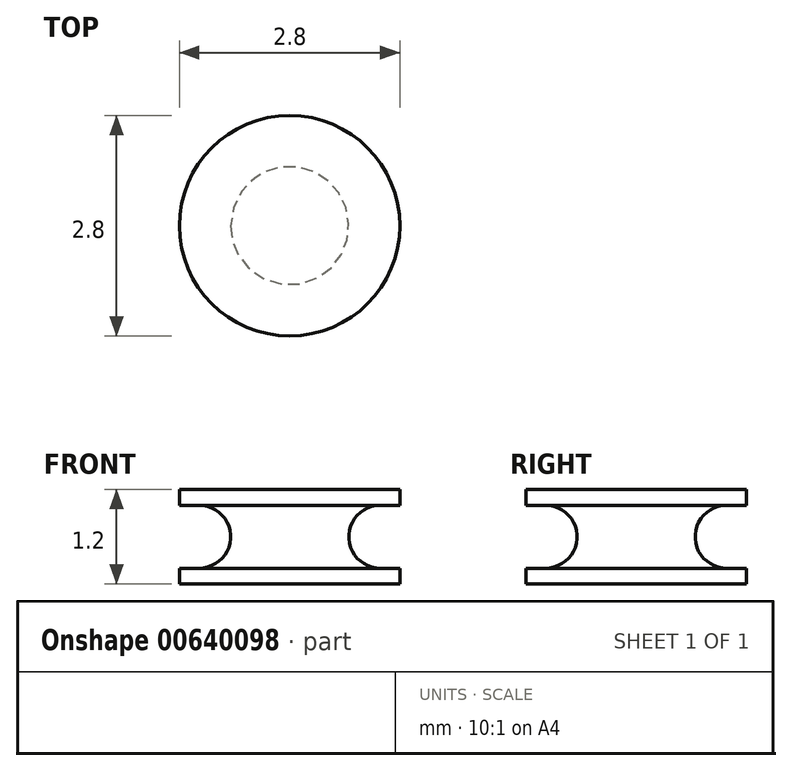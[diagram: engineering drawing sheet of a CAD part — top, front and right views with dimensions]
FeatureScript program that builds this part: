
annotation { "Feature Type Name" : "Feature", "Feature Type Description" : "" }
export const myFeature = defineFeature(function(context is Context, id is Id, definition is map)
    precondition{}
    {
        {
            var Q0;
            Q0=qCreatedBy(makeId("Front.planeOp"),FACE);
            var sketch = newSketch(context, id + "F0", { "sketchPlane" : qUnion([Q0])});
            skLineSegment(sketch, "E0.top", {"start": v(0, 0.6) * mm, "end": v(1.4, 0.6) * mm});
            skLineSegment(sketch, "E0.left", {"start": v(0, 0) * mm, "end": v(0, 0.6) * mm});
            skLineSegment(sketch, "E0.right", {"start": v(1.4, 0.4) * mm, "end": v(1.4, 0.6) * mm});
            skArc(sketch, "E1", {"start": v(1.15, 0.4) * mm, "mid": v(0.87, 0.28) * mm, "end": v(0.75, 0) * mm});
            skLineSegment(sketch, "E2", {"start": v(1.15, 0.4) * mm, "end": v(1.4, 0.4) * mm});
            skLineSegment(sketch, "E3.MirrorCS", {"start": v(0, -0.6) * mm, "end": v(1.4, -0.6) * mm});
            skLineSegment(sketch, "E4.MirrorCS", {"start": v(0, 0) * mm, "end": v(0, -0.6) * mm});
            skLineSegment(sketch, "E5.MirrorCS", {"start": v(1.15, -0.4) * mm, "end": v(1.4, -0.4) * mm});
            skArc(sketch, "E6.MirrorCS", {"start": v(1.15, -0.4) * mm, "mid": v(0.87, -0.28) * mm, "end": v(0.75, 0) * mm});
            skLineSegment(sketch, "E7.MirrorCS", {"start": v(1.4, -0.4) * mm, "end": v(1.4, -0.6) * mm});
            skSolve(sketch);
        }
        {
            var Q0;
            Q0=makeQuery(id+"F0.imprint","IMPRINT",FACE,{"disambiguationData":[TD([[makeQuery(id+"F0.imprint","IMPRINT",EDGE,{"derivedFrom":sQuery(id+"F0.wireOp",EDGE,"E0.top")}),-1.0]])]});
            var Q1;
            Q1=sQuery(id+"F0.wireOp",EDGE,"E0.left");
            revolve(context, id + "F1", {"entities" : qUnion([Q0]), "axis" : qUnion([Q1]), "revolveType" : RevolveType.FULL});
        }
    });
